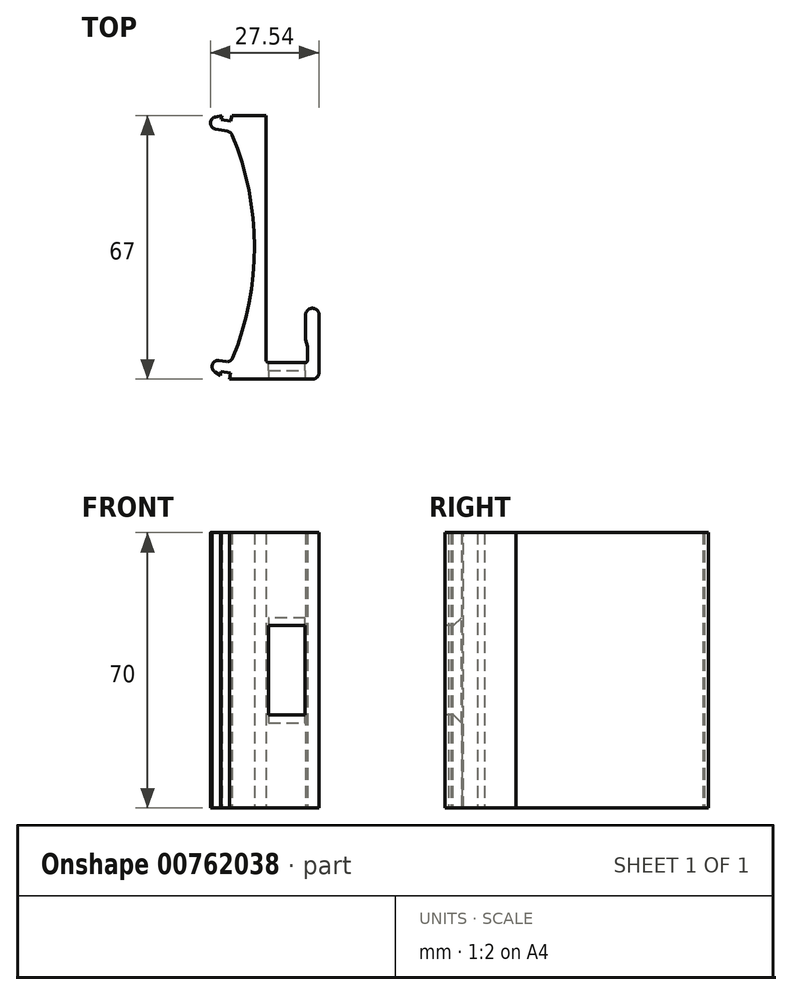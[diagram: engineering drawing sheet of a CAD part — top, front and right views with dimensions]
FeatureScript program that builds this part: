
annotation { "Feature Type Name" : "Feature", "Feature Type Description" : "" }
export const myFeature = defineFeature(function(context is Context, id is Id, definition is map)
    precondition{}
    {
        {
            var Q0;
            Q0=qCreatedBy(makeId("Top.planeOp"),FACE);
            var sketch = newSketch(context, id + "F0", { "sketchPlane" : qUnion([Q0])});
            skLineSegment(sketch, "E0.bottom", {"start": v(0, 33.5) * mm, "end": v(-9, 33.5) * mm});
            skLineSegment(sketch, "E0.top", {"start": v(0, -33.5) * mm, "end": v(-9, -33.5) * mm});
            skLineSegment(sketch, "E0.left", {"start": v(0, 33.5) * mm, "end": v(0, -33.5) * mm});
            skLineSegment(sketch, "E0.right", {"start": v(-9, 32) * mm, "end": v(-9, -33.5) * mm});
            skPoint(sketch, "E0.middle", {"position": v(-4.5, 0) * mm});
            skLineSegment(sketch, "E1", {"start": v(-9, 32) * mm, "end": v(0, 32) * mm});
            skLineSegment(sketch, "E2", {"start": v(-9, 29.3) * mm, "end": v(0, 29.3) * mm});
            skLineSegment(sketch, "E3.MirrorCS", {"start": v(-9, -29.3) * mm, "end": v(0, -29.3) * mm});
            skLineSegment(sketch, "E4.MirrorCS", {"start": v(-9, -32) * mm, "end": v(0, -32) * mm});
            skArc(sketch, "E5", {"start": v(-9, -29.3) * mm, "mid": v(-2.97, 0) * mm, "end": v(-9, 29.3) * mm});
            skLineSegment(sketch, "E6", {"start": v(-9, 32) * mm, "end": v(-9, 33.5) * mm});
            skPoint(sketch, "E7.orphan", {"position": v(-9, 33.5) * mm});
            skLineSegment(sketch, "E8", {"start": v(-9, -32) * mm, "end": v(-13.92, -31.1) * mm});
            skLineSegment(sketch, "E9", {"start": v(-9, 32) * mm, "end": v(-13.92, 32.9) * mm});
            skLineSegment(sketch, "E10", {"start": v(-13.92, -31.1) * mm, "end": v(-13.44, -28.48) * mm});
            skLineSegment(sketch, "E11", {"start": v(-9, -29.3) * mm, "end": v(-13.44, -28.48) * mm});
            skLineSegment(sketch, "E12", {"start": v(-13.92, 32.9) * mm, "end": v(-14.4, 30.3) * mm});
            skLineSegment(sketch, "E13", {"start": v(-9, 29.3) * mm, "end": v(-14.4, 30.3) * mm});
            skLineSegment(sketch, "E14", {"start": v(-13.92, -31.1) * mm, "end": v(-11.63, -32.53) * mm});
            skLineSegment(sketch, "E15", {"start": v(-11.63, -32.53) * mm, "end": v(-11.46, -31.55) * mm});
            skLineSegment(sketch, "E16", {"start": v(-13.92, 32.9) * mm, "end": v(-11.27, 33.43) * mm});
            skLineSegment(sketch, "E17", {"start": v(-11.27, 33.43) * mm, "end": v(-11.46, 32.45) * mm});
            skLineSegment(sketch, "E18", {"start": v(-9, 32) * mm, "end": v(-8.71, 33.5) * mm});
            skLineSegment(sketch, "E19", {"start": v(-9, -32) * mm, "end": v(-9.26, -33.5) * mm});
            skLineSegment(sketch, "E20", {"start": v(-9.26, -33.5) * mm, "end": v(-9, -33.5) * mm});
            skLineSegment(sketch, "E21", {"start": v(0, -33.5) * mm, "end": v(13.4, -33.5) * mm});
            skLineSegment(sketch, "E22", {"start": v(13.4, -33.5) * mm, "end": v(13.4, -15.5) * mm});
            skLineSegment(sketch, "E23", {"start": v(0, -29.3) * mm, "end": v(10.5, -29.3) * mm});
            skLineSegment(sketch, "E24", {"start": v(10.5, -29.3) * mm, "end": v(10.5, -15.95) * mm});
            skLineSegment(sketch, "E25", {"start": v(10.8, -15.5) * mm, "end": v(13.4, -15.5) * mm});
            skLineSegment(sketch, "E26", {"start": v(10, -16.72) * mm, "end": v(10, -23.38) * mm});
            skLineSegment(sketch, "E27", {"start": v(10.5, -22.24) * mm, "end": v(10.5, -15.95) * mm});
            skLineSegment(sketch, "E28", {"start": v(10.8, -15.5) * mm, "end": v(10, -16.72) * mm});
            skPoint(sketch, "E29.orphan", {"position": v(10.5, -15.5) * mm});
            skLineSegment(sketch, "E30", {"start": v(10, -23.38) * mm, "end": v(10.5, -25.21) * mm});
            skSolve(sketch);
        }
        {
            var Q0;
            {var subQ0=sQuery(id+"F0.wireOp",EDGE,"E10");Q0=makeQuery(id+"F0.imprint","IMPRINT",FACE,{"disambiguationData":[TD([[makeQuery(id+"F0.imprint","IMPRINT",EDGE,{"derivedFrom":subQ0}),-1.0]])]});}
            var Q1;
            {var subQ0=sQuery(id+"F0.wireOp",EDGE,"E3.MirrorCS");Q1=makeQuery(id+"F0.imprint","IMPRINT",FACE,{"disambiguationData":[TD([[makeQuery(id+"F0.imprint","IMPRINT",EDGE,{"derivedFrom":subQ0}),-1.0]])]});}
            var Q2;
            {var subQ2=sQuery(id+"F0.wireOp",EDGE,"E19");Q2=makeQuery(id+"F0.imprint","IMPRINT",FACE,{"disambiguationData":[TD([[makeQuery(id+"F0.imprint","IMPRINT",EDGE,{"derivedFrom":subQ2}),1.0]])]});}
            var Q3;
            {var subQ0=sQuery(id+"F0.wireOp",EDGE,"E0.top");Q3=makeQuery(id+"F0.imprint","IMPRINT",FACE,{"disambiguationData":[TD([[makeQuery(id+"F0.imprint","IMPRINT",EDGE,{"derivedFrom":subQ0}),-1.0]])]});}
            var Q4;
            {var subQ0=sQuery(id+"F0.wireOp",EDGE,"E14");Q4=makeQuery(id+"F0.imprint","IMPRINT",FACE,{"disambiguationData":[TD([[makeQuery(id+"F0.imprint","IMPRINT",EDGE,{"derivedFrom":subQ0}),1.0]])]});}
            var Q5;
            {var subQ0=sQuery(id+"F0.wireOp",EDGE,"E2");Q5=makeQuery(id+"F0.imprint","IMPRINT",FACE,{"disambiguationData":[TD([[makeQuery(id+"F0.imprint","IMPRINT",EDGE,{"derivedFrom":subQ0}),-1.0]])]});}
            var Q6;
            {var subQ0=sQuery(id+"F0.wireOp",EDGE,"E1");Q6=makeQuery(id+"F0.imprint","IMPRINT",FACE,{"disambiguationData":[TD([[makeQuery(id+"F0.imprint","IMPRINT",EDGE,{"derivedFrom":subQ0}),-1.0]])]});}
            var Q7;
            {var subQ4=sQuery(id+"F0.wireOp",EDGE,"E1");Q7=makeQuery(id+"F0.imprint","IMPRINT",FACE,{"disambiguationData":[TD([[makeQuery(id+"F0.imprint","IMPRINT",EDGE,{"derivedFrom":subQ4}),1.0]])]});}
            var Q8;
            {var subQ0=sQuery(id+"F0.wireOp",EDGE,"E12");Q8=makeQuery(id+"F0.imprint","IMPRINT",FACE,{"disambiguationData":[TD([[makeQuery(id+"F0.imprint","IMPRINT",EDGE,{"derivedFrom":subQ0}),1.0]])]});}
            var Q9;
            {var subQ0=sQuery(id+"F0.wireOp",EDGE,"E16");Q9=makeQuery(id+"F0.imprint","IMPRINT",FACE,{"disambiguationData":[TD([[makeQuery(id+"F0.imprint","IMPRINT",EDGE,{"derivedFrom":subQ0}),-1.0]])]});}
            var Q10;
            {var subQ0=sQuery(id+"F0.wireOp",EDGE,"E21");Q10=makeQuery(id+"F0.imprint","IMPRINT",FACE,{"disambiguationData":[TD([[makeQuery(id+"F0.imprint","IMPRINT",EDGE,{"derivedFrom":subQ0}),1.0]])]});}
            var Q11;
            {var subQ1=sQuery(id+"F0.wireOp",EDGE,"E26");Q11=makeQuery(id+"F0.imprint","IMPRINT",FACE,{"disambiguationData":[TD([[makeQuery(id+"F0.imprint","IMPRINT",EDGE,{"derivedFrom":subQ1}),1.0]])]});}
            extrude(context, id + "F1", {"entities" : qUnion([Q0, Q1, Q2, Q3, Q4, Q5, Q6, Q7, Q8, Q9, Q10, Q11]), "depth" : 70 * mm, "offsetDistance" : 25 * mm});
        }
        {
            var Q0;
            Q0=makeQuery(id+"F1.opExtrude","SWEPT_EDGE",EDGE,{"disambiguationData":[OSD([sQuery(id+"F0.wireOp",EDGE,"E12"),sQuery(id+"F0.wireOp",EDGE,"E13")])]});
            var Q1;
            Q1=makeQuery(id+"F1.opExtrude","SWEPT_EDGE",EDGE,{"disambiguationData":[OSD([sQuery(id+"F0.wireOp",EDGE,"E0.right"),sQuery(id+"F0.wireOp",EDGE,"E2"),sQuery(id+"F0.wireOp",EDGE,"E5"),sQuery(id+"F0.wireOp",EDGE,"E13")])]});
            var Q2;
            Q2=makeQuery(id+"F1.opExtrude","SWEPT_EDGE",EDGE,{"disambiguationData":[OSD([sQuery(id+"F0.wireOp",EDGE,"E10"),sQuery(id+"F0.wireOp",EDGE,"E11")])]});
            var Q3;
            Q3=makeQuery(id+"F1.opExtrude","SWEPT_EDGE",EDGE,{"disambiguationData":[OSD([sQuery(id+"F0.wireOp",EDGE,"E0.right"),sQuery(id+"F0.wireOp",EDGE,"E3.MirrorCS"),sQuery(id+"F0.wireOp",EDGE,"E5"),sQuery(id+"F0.wireOp",EDGE,"E11")])]});
            var Q4;
            Q4=makeQuery(id+"F1.opExtrude","SWEPT_EDGE",EDGE,{"disambiguationData":[OSD([sQuery(id+"F0.wireOp",EDGE,"E8"),sQuery(id+"F0.wireOp",EDGE,"E10"),sQuery(id+"F0.wireOp",EDGE,"E14")])]});
            var Q5;
            Q5=makeQuery(id+"F1.opExtrude","SWEPT_EDGE",EDGE,{"disambiguationData":[OSD([sQuery(id+"F0.wireOp",EDGE,"E9"),sQuery(id+"F0.wireOp",EDGE,"E12"),sQuery(id+"F0.wireOp",EDGE,"E16")])]});
            fillet(context, id + "F2", {"entities" : qUnion([Q0, Q1, Q2, Q3, Q4, Q5]), "radius" : 1.55 * mm, "tangentPropagation" : true, "allowEdgeOverflow" : false});
        }
        {
            var Q0;
            Q0=makeQuery(id+"F1.opExtrude","SWEPT_FACE",FACE,{"disambiguationData":[OSD([sQuery(id+"F0.wireOp",EDGE,"E0.top"),sQuery(id+"F0.wireOp",EDGE,"E20"),sQuery(id+"F0.wireOp",EDGE,"E21")])]});
            var sketch = newSketch(context, id + "F3", { "sketchPlane" : qUnion([Q0])});
            skLineSegment(sketch, "E31", {"start": v(9.9, 46.38) * mm, "end": v(9.9, 23.62) * mm});
            skLineSegment(sketch, "E32", {"start": v(9.9, 23.62) * mm, "end": v(0.6, 23.62) * mm});
            skLineSegment(sketch, "E33", {"start": v(0.6, 23.62) * mm, "end": v(0.6, 46.38) * mm});
            skLineSegment(sketch, "E34", {"start": v(0.6, 46.38) * mm, "end": v(9.9, 46.38) * mm});
            skSolve(sketch);
        }
        {
            var Q0;
            Q0=makeQuery(id+"F3.imprint","IMPRINT",FACE,{"disambiguationData":[TD([[makeQuery(id+"F3.imprint","IMPRINT",EDGE,{"derivedFrom":sQuery(id+"F3.wireOp",EDGE,"WwaaJVhM-k0OZ-fXfq-VhrI-MonXxmD6BPsM")}),-1.0]])]});
            var Q1;
            Q1=makeQuery(id+"F3.imprint","IMPRINT",FACE,{"disambiguationData":[TD([[makeQuery(id+"F3.imprint","IMPRINT",EDGE,{"derivedFrom":sQuery(id+"F3.wireOp",EDGE,"E31")}),-1.0]])]});
            extrude(context, id + "F4", {"entities" : qUnion([Q0, Q1]), "operationType" : NewBodyOperationType.REMOVE, "oppositeDirection" : true, "depth" : 5 * mm, "offsetDistance" : 25 * mm});
        }
        {
            var Q0;
            Q0=makeQuery(id+"F4.boolean.opBoolean","COPY",EDGE,{"derivedFrom":makeQuery(id+"F4.opExtrude","CAP_EDGE",EDGE,{"disambiguationData":[OSD([sQuery(id+"F3.wireOp",EDGE,"E34")])],"isStart":true})});
            var Q1;
            Q1=makeQuery(id+"F4.boolean.opBoolean","COPY",EDGE,{"derivedFrom":makeQuery(id+"F4.opExtrude","CAP_EDGE",EDGE,{"disambiguationData":[OSD([sQuery(id+"F3.wireOp",EDGE,"E32")])],"isStart":true})});
            var Q2;
            Q2=makeQuery(id+"F4.boolean.opBoolean","INTERSECT",EDGE,{"derivedFrom":[makeQuery(id+"F1.opExtrude","SWEPT_FACE",FACE,{"disambiguationData":[OSD([sQuery(id+"F0.wireOp",EDGE,"E23")])]}),makeQuery(id+"F4.opExtrude","SWEPT_FACE",FACE,{"disambiguationData":[OSD([sQuery(id+"F3.wireOp",EDGE,"E32")])]})]});
            var Q3;
            Q3=makeQuery(id+"F4.boolean.opBoolean","INTERSECT",EDGE,{"derivedFrom":[makeQuery(id+"F1.opExtrude","SWEPT_FACE",FACE,{"disambiguationData":[OSD([sQuery(id+"F0.wireOp",EDGE,"E23")])]}),makeQuery(id+"F4.opExtrude","SWEPT_FACE",FACE,{"disambiguationData":[OSD([sQuery(id+"F3.wireOp",EDGE,"E34")])]})]});
            chamfer(context, id + "F5", {"entities" : qUnion([Q0, Q1, Q2, Q3]), "width" : 2 * mm, "tangentPropagation" : true});
        }
        {
            var Q0;
            Q0=makeQuery(id+"F1.opExtrude","SWEPT_EDGE",EDGE,{"disambiguationData":[OSD([sQuery(id+"F0.wireOp",EDGE,"E0.left"),sQuery(id+"F0.wireOp",EDGE,"E3.MirrorCS"),sQuery(id+"F0.wireOp",EDGE,"E23")])]});
            var Q1;
            Q1=makeQuery(id+"F1.opExtrude","SWEPT_EDGE",EDGE,{"disambiguationData":[OSD([sQuery(id+"F0.wireOp",EDGE,"E23"),sQuery(id+"F0.wireOp",EDGE,"E24")])]});
            fillet(context, id + "F6", {"entities" : qUnion([Q0, Q1]), "radius" : 0.6 * mm, "tangentPropagation" : true, "allowEdgeOverflow" : false});
        }
        {
            var Q0;
            Q0=makeQuery(id+"F1.opExtrude","SWEPT_EDGE",EDGE,{"disambiguationData":[OSD([sQuery(id+"F0.wireOp",EDGE,"E25"),sQuery(id+"F0.wireOp",EDGE,"E28")])]});
            var Q1;
            Q1=makeQuery(id+"F1.opExtrude","SWEPT_EDGE",EDGE,{"disambiguationData":[OSD([sQuery(id+"F0.wireOp",EDGE,"E22"),sQuery(id+"F0.wireOp",EDGE,"E25")])]});
            var Q2;
            Q2=makeQuery(id+"F1.opExtrude","SWEPT_EDGE",EDGE,{"disambiguationData":[OSD([sQuery(id+"F0.wireOp",EDGE,"E26"),sQuery(id+"F0.wireOp",EDGE,"E28")])]});
            var Q3;
            Q3=makeQuery(id+"F1.opExtrude","SWEPT_EDGE",EDGE,{"disambiguationData":[OSD([sQuery(id+"F0.wireOp",EDGE,"E21"),sQuery(id+"F0.wireOp",EDGE,"E22")])]});
            fillet(context, id + "F7", {"entities" : qUnion([Q0, Q1, Q2, Q3]), "radius" : 1.6 * mm, "tangentPropagation" : true, "allowEdgeOverflow" : false});
        }
    });
